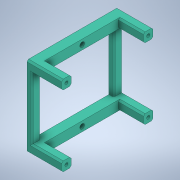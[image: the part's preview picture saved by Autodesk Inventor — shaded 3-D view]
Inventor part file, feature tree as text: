
AUTODESK INVENTOR PART (.ipt)
format: ipt  version: 2020 (Build 240168000, 168)  size: 191,488 bytes
history: native  units: mm
features: extrude x4, sketch x4, pattern_linear x1, chamfer x1
ambient origin geometry x8: Origin, YZ Plane, XZ Plane, XY Plane, X Axis, Y Axis, Z Axis, Center Point
bodies: Solid1 (feature_tree)
feature tree (10):
  extrude  "Extrusion1"  Depth=6.0mm
  extrude  "Extrusion2"  Depth=22.0mm
  extrude  "Extrusion3"  Depth=6.0mm
  pattern_linear  "Rectangular Pattern2"  Spacing1=3.0mm  [1 undecoded]
  extrude  "Extrusion4"  TaperAngle=0.0deg  [1 undecoded]
  chamfer  "Chamfer3"  Distance=45.0mm
  sketch  "Sketch1"  dims[d0=6.0mm d1=6.0mm]
  sketch  "Sketch2"  dims[d2=58.0mm d3=22.0mm]
  sketch  "Sketch3"  dims[d4=6.0mm d5=0.0mm d6=2.0mm]
  sketch  "Sketch5"  dims[d7=12.0mm d8=0.0mm d9=3.0mm d10=0.0mm d11=0.0mm d21=20.0mm d23=45.0mm d24=3.0mm d25=0.0mm d26=1.0mm d27=2.0mm d28=45.0deg]
note: 2 required parameter values undecoded (feature->parameter linkage not recoverable at this tier; creation-order binding heuristic only, values carry confidence <= 0.55)
